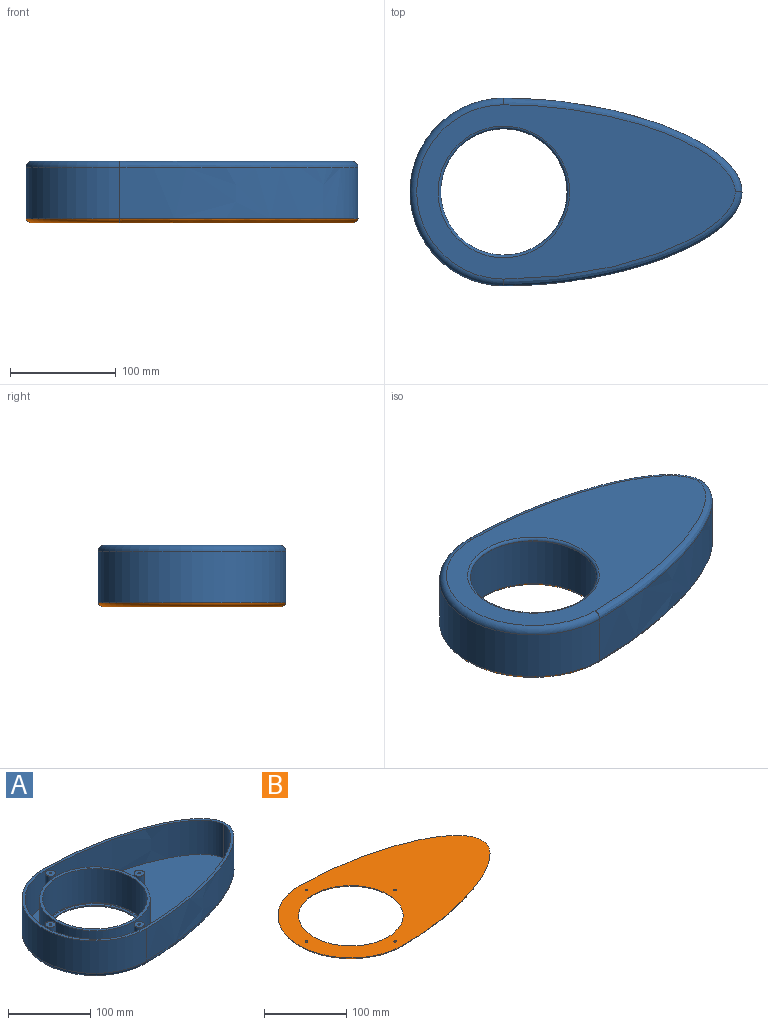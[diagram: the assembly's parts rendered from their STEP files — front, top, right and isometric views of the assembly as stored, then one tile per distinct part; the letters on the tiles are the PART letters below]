
ASSEMBLY  parts=2 mates=1
PART A: 34 faces, bbox 321.1x192.1x54.6 mm
  f0: plane 313.82x177.48mm, normal (0,0,1), area 2967.4mm2, adj f2,f3,f4,f7,f8,f9
  f1: plane 134.62x134.62mm, normal (0,0,1), area 1565.7mm2, adj f5,f10
  f2: extruded ~225.08x88.74mm, area 12358.4mm2, adj f0,f3,f4,f30
  f3: cylinder r=88.74mm len=177.48mm, axis (0,0,-1), area 13453.9mm2, adj f0,f2,f4,f28
  f4: extruded ~225.08x88.74mm, area 12358.4mm2, adj f0,f2,f3,f29
  f5: cylinder r=63.5mm len=127mm, axis (0,0,-1), area 20268.3mm2, adj f1,f31
  f6: plane 301.12x164.78mm, normal (0,0,-1), area 25887.9mm2, adj f28,f29,f30,f32
  f7: extruded ~221.27x84.93mm, area 12704.8mm2, adj f0,f8,f9,f11
  f8: cylinder r=84.93mm len=169.86mm, axis (0,0,-1), area 13553.9mm2, adj f0,f7,f9,f11
  f9: extruded ~221.27x84.93mm, area 12704.8mm2, adj f0,f7,f8,f11
  f10: cylinder r=67.31mm len=134.62mm, axis (0,0,-1), area 21484.4mm2, adj f1,f11
  f11: plane 306.2x169.86mm, normal (0,0,1), area 25242.5mm2, adj f7,f8,f9,f10,f13,f17,f21,f25
  f12: cylinder r=1.59mm len=50.8mm, axis (0,0,-1), area 506.7mm2, adj f14,f15
  f13: cylinder r=6.35mm len=50.8mm, axis (0,0,-1), area 2026.8mm2, adj f11,f14
  f14: plane 12.7x12.7mm, normal (0,0,1), area 118.8mm2, adj f12,f13
  f15: plane 3.18x3.18mm, normal (0,0,1), area 7.9mm2, adj f12
  f16: cylinder r=1.59mm len=50.8mm, axis (0,0,-1), area 506.7mm2, adj f18,f19
  f17: cylinder r=6.35mm len=50.8mm, axis (0,0,-1), area 2026.8mm2, adj f11,f18
  f18: plane 12.7x12.7mm, normal (0,0,1), area 118.8mm2, adj f16,f17
  f19: plane 3.18x3.18mm, normal (0,0,1), area 7.9mm2, adj f16
  f20: cylinder r=1.59mm len=50.8mm, axis (0,0,-1), area 506.7mm2, adj f22,f23
  f21: cylinder r=6.35mm len=50.8mm, axis (0,0,-1), area 2026.8mm2, adj f11,f22
  f22: plane 12.7x12.7mm, normal (0,0,1), area 118.8mm2, adj f20,f21
  f23: plane 3.18x3.18mm, normal (0,0,1), area 7.9mm2, adj f20
  f24: cylinder r=1.59mm len=50.8mm, axis (0,0,-1), area 506.7mm2, adj f26,f27
  f25: cylinder r=6.35mm len=50.8mm, axis (0,0,-1), area 2026.8mm2, adj f11,f26
  f26: plane 12.7x12.7mm, normal (0,0,1), area 118.8mm2, adj f24,f25
  f27: plane 3.18x3.18mm, normal (0,0,1), area 7.9mm2, adj f24
  f28: torus R=82.39mm, axis (0,0,1), area 2708.4mm2, adj f3,f6,f29,f30
  f29: bspline ~319.51x112.34mm, area 2518mm2, adj f4,f6,f28,f30
  f30: bspline ~319.51x112.34mm, area 2518.1mm2, adj f2,f6,f28,f29
  f31: plane 127x127mm, normal (0,0,1), area 634.3mm2, adj f5,f33
  f32: torus R=62.23mm, axis (0,0,1), area 1519.5mm2, adj f6,f33
  f33: torus R=61.89mm, axis (0,0,1), area 1014.1mm2, adj f31,f32
PART B: 10 faces, bbox 321.7x193.2x6.4 mm
  f0: plane 313.83x177.48mm, normal (0,0,1), area 30251.9mm2, adj f2,f3,f4,f5,f6,f7,f8,f9
  f1: plane 302.19x165.84mm, normal (0,0,-1), area 23328.3mm2, adj f2,f3,f4,f5,f6,f7,f8,f9
  f2: cylinder r=1.59mm len=3.81mm, axis (0,0,-1), area 38mm2, adj f0,f1
  f3: cylinder r=1.59mm len=3.81mm, axis (0,0,-1), area 38mm2, adj f0,f1
  f4: cylinder r=1.59mm len=3.81mm, axis (0,0,-1), area 38mm2, adj f0,f1
  f5: cylinder r=1.59mm len=3.81mm, axis (0,0,-1), area 38mm2, adj f0,f1
  f6: torus R=82.92mm, axis (0,0,-1), area 1993.6mm2, adj f0,f1,f7,f8
  f7: bspline ~228.83x89.11mm, area 1855.9mm2, adj f0,f1,f6,f8
  f8: bspline ~228.83x89.11mm, area 1855.9mm2, adj f0,f1,f6,f7
  f9: torus R=69.32mm, axis (0,0,1), area 3054.3mm2, adj f0,f1
PLACE A rot(axis=(-1,0,0),180deg) t=(74.27,27.59,-34.36)mm
PLACE B t=(74.27,27.59,-92.78)mm
MATE fastened A.f5 <-> B.f9  axis (0,0,-1) through (74.27,27.59,-88.97)mm
